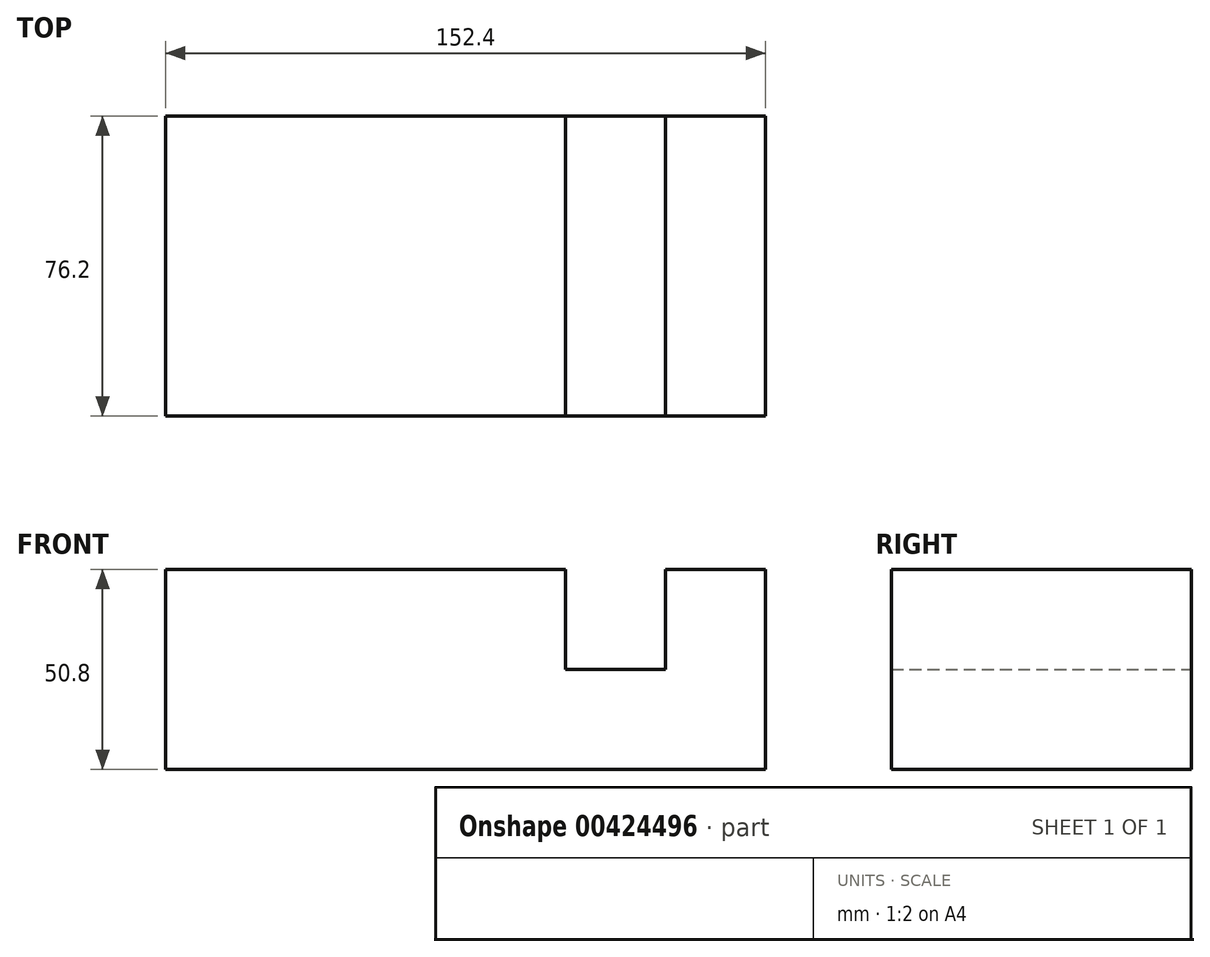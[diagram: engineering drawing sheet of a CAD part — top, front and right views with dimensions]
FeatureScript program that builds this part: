
annotation { "Feature Type Name" : "Feature", "Feature Type Description" : "" }
export const myFeature = defineFeature(function(context is Context, id is Id, definition is map)
    precondition{}
    {
        {
            var Q0;
            Q0=qCreatedBy(makeId("Front.planeOp"),FACE);
            var sketch = newSketch(context, id + "F0", { "sketchPlane" : qUnion([Q0])});
            skLineSegment(sketch, "E0", {"start": v(0, 0) * mm, "end": v(152.4, 0) * mm});
            skLineSegment(sketch, "E1", {"start": v(0, 0) * mm, "end": v(0, 50.8) * mm});
            skLineSegment(sketch, "E2", {"start": v(0, 50.8) * mm, "end": v(101.6, 50.8) * mm});
            skLineSegment(sketch, "E3", {"start": v(101.6, 50.8) * mm, "end": v(101.6, 25.4) * mm});
            skLineSegment(sketch, "E4", {"start": v(101.6, 25.4) * mm, "end": v(127, 25.4) * mm});
            skLineSegment(sketch, "E5", {"start": v(127, 25.4) * mm, "end": v(127, 50.8) * mm});
            skLineSegment(sketch, "E6", {"start": v(127, 50.8) * mm, "end": v(152.4, 50.8) * mm});
            skLineSegment(sketch, "E7", {"start": v(152.4, 50.8) * mm, "end": v(152.4, 0) * mm});
            skSolve(sketch);
        }
        {
            var Q0;
            Q0 = qSketchRegion(id + "F0", true);
            extrude(context, id + "F1", {"entities" : qUnion([Q0]), "depth" : 76.2 * mm});
        }
    });
